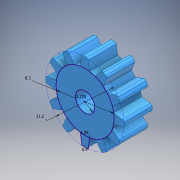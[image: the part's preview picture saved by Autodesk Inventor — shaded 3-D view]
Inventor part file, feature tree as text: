
AUTODESK INVENTOR PART (.ipt)
format: ipt  version: 2018 (Build 220112000, 112)  size: 198,656 bytes
history: native  units: mm
features: extrude x3, sketch x1, fillet x1, pattern_circular x1
ambient origin geometry x8: Origin, YZ Plane, XZ Plane, XY Plane, X Axis, Y Axis, Z Axis, Center Point
bodies: Solid1 (feature_tree)
feature tree (6):
  sketch  "Sketch1"  dims[d1=11.2mm d2=8.3mm d3=0.9mm d4=1.35mm d5=4.0mm d6=0.0mm d7=4.0mm d8=0.0mm d9=120.0mm d10=360.0deg d12=0.3mm d13=2.725mm d14=4.0mm d15=0.0mm]
  extrude  "Extrusion1"  Depth=4.0mm
  extrude  "Extrusion2"  Depth=4.0mm
  fillet  "Fillet1"  Radius=1.35mm
  pattern_circular  "Circular Pattern1"  [2 undecoded]
  extrude  "Extrusion3"  Depth=4.0mm TaperAngle=0.0deg
note: 2 required parameter values undecoded (feature->parameter linkage not recoverable at this tier; creation-order binding heuristic only, values carry confidence <= 0.55)
